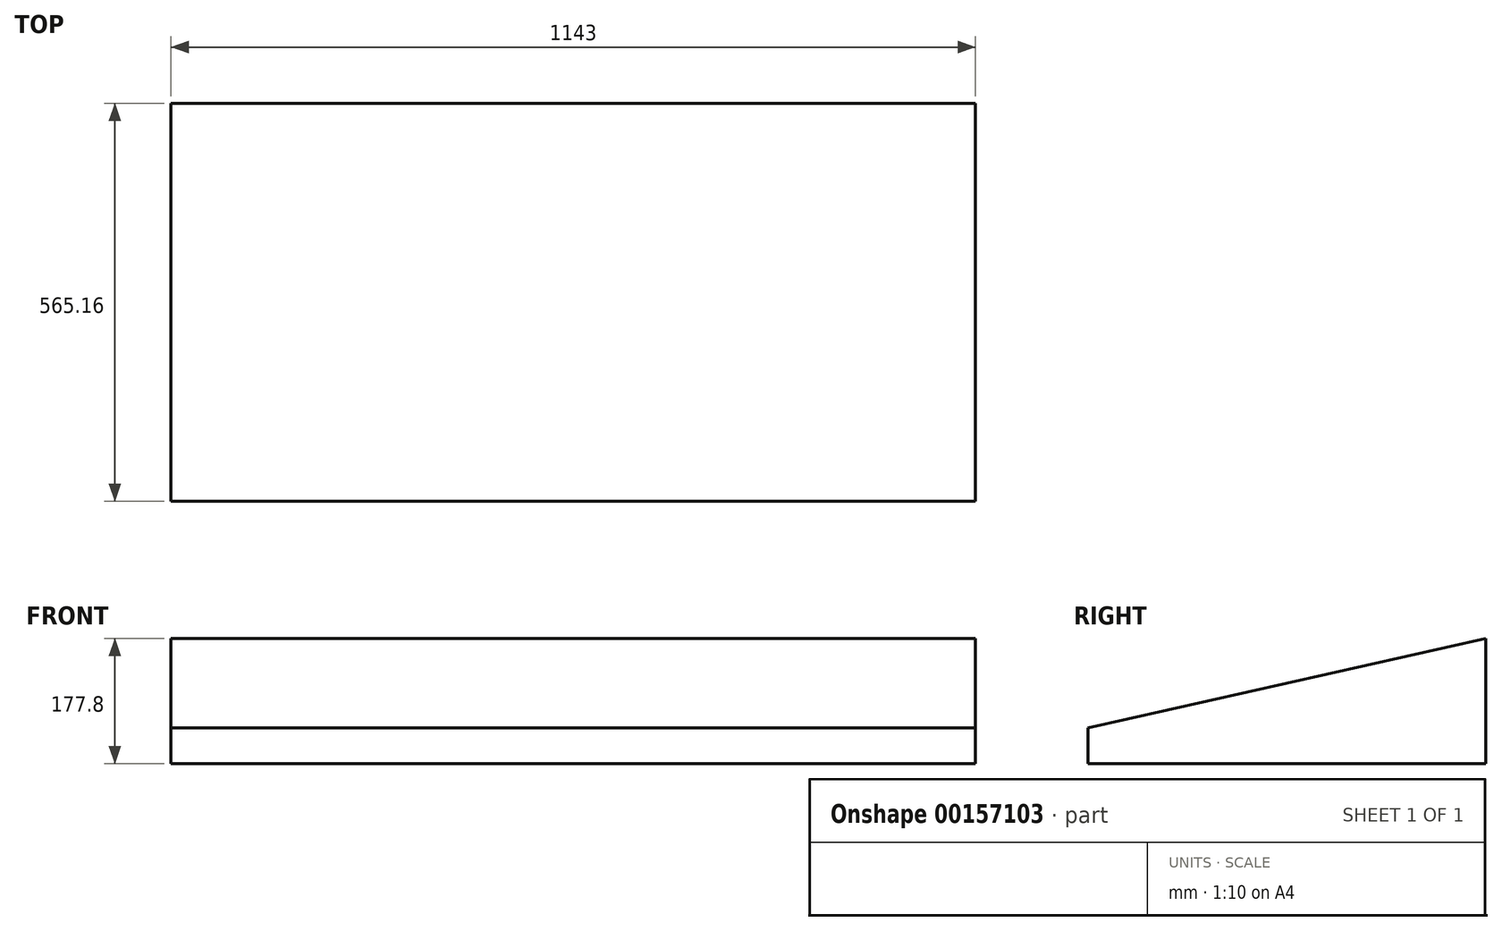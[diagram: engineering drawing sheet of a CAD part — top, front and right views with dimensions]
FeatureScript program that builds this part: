
annotation { "Feature Type Name" : "Feature", "Feature Type Description" : "" }
export const myFeature = defineFeature(function(context is Context, id is Id, definition is map)
    precondition{}
    {
        {
            var Q0;
            Q0=qCreatedBy(makeId("Top.planeOp"),FACE);
            var sketch = newSketch(context, id + "F0", { "sketchPlane" : qUnion([Q0])});
            skLineSegment(sketch, "E0.bottom", {"start": v(571.5, 282.58) * mm, "end": v(-571.5, 282.58) * mm});
            skLineSegment(sketch, "E0.top", {"start": v(571.5, -282.58) * mm, "end": v(-571.5, -282.58) * mm});
            skLineSegment(sketch, "E0.left", {"start": v(571.5, 282.58) * mm, "end": v(571.5, -282.58) * mm});
            skLineSegment(sketch, "E0.right", {"start": v(-571.5, 282.58) * mm, "end": v(-571.5, -282.58) * mm});
            skPoint(sketch, "E0.middle", {"position": v(0, 0) * mm});
            skSolve(sketch);
        }
        {
            var Q0;
            Q0=makeQuery(id+"F0.imprint","IMPRINT",FACE,{"disambiguationData":[TD([[makeQuery(id+"F0.imprint","IMPRINT",EDGE,{"derivedFrom":sQuery(id+"F0.wireOp",EDGE,"E0.bottom")}),1.0]])]});
            extrude(context, id + "F1", {"entities" : qUnion([Q0]), "depth" : 228.6 * mm});
        }
        {
            var Q0;
            Q0=makeQuery(id+"F1.opExtrude","SWEPT_FACE",FACE,{"disambiguationData":[OSD([sQuery(id+"F0.wireOp",EDGE,"E0.right")])]});
            var sketch = newSketch(context, id + "F2", { "sketchPlane" : qUnion([Q0])});
            skPoint(sketch, "E1", {"position": v(282.57, 50.8) * mm});
            skPoint(sketch, "E2", {"position": v(-282.58, 177.8) * mm});
            skLineSegment(sketch, "E3", {"start": v(-282.58, 177.8) * mm, "end": v(282.57, 50.8) * mm});
            skSolve(sketch);
        }
        {
            var Q0;
            {var subQ0=sQuery(id+"F2.wireOp",EDGE,"E3");Q0=makeQuery(id+"F2.imprint","IMPRINT",FACE,{"disambiguationData":[TD([[makeQuery(id+"F2.imprint","IMPRINT",EDGE,{"derivedFrom":subQ0}),1.0]])]});}
            extrude(context, id + "F3", {"entities" : qUnion([Q0]), "operationType" : NewBodyOperationType.REMOVE, "oppositeDirection" : true, "depth" : 1358.16 * mm});
        }
    });
